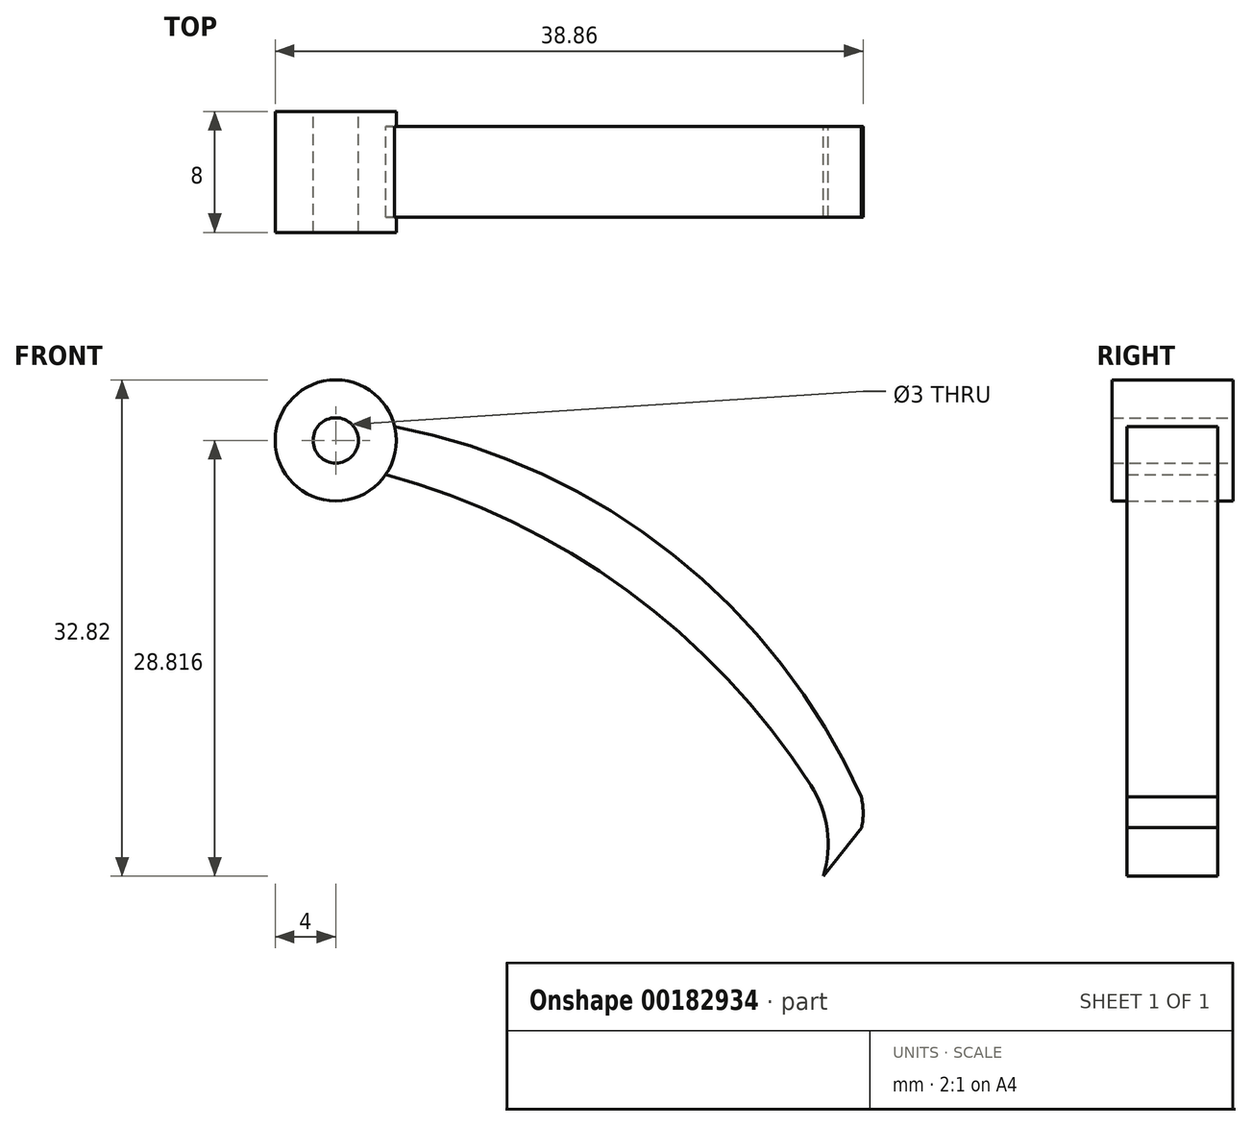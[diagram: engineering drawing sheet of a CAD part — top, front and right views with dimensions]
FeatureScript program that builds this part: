
annotation { "Feature Type Name" : "Feature", "Feature Type Description" : "" }
export const myFeature = defineFeature(function(context is Context, id is Id, definition is map)
    precondition{}
    {
        {
            var Q0;
            Q0=qCreatedBy(makeId("Front.planeOp"),FACE);
            var sketch = newSketch(context, id + "F0", { "sketchPlane" : qUnion([Q0])});
            skPoint(sketch, "E0.center", {"position": v(-0.03, 0) * mm});
            skLineSegment(sketch, "E1", {"start": v(0, 0) * mm, "end": v(-0.03, 0) * mm});
            skLineSegment(sketch, "E2", {"start": v(-0.03, 0) * mm, "end": v(0, 0.04) * mm});
            skArc(sketch, "E3", {"start": v(31.4, 46.86) * mm, "mid": v(19.25, 59.73) * mm, "end": v(3.3, 67.38) * mm});
            skPoint(sketch, "E3.startSnap0", {"position": v(33.76, 42.76) * mm});
            skLineSegment(sketch, "E4", {"start": v(32.2, 40.8) * mm, "end": v(32.2, 40.82) * mm});
            skLineSegment(sketch, "E5.trimOffspring", {"start": v(32.2, 40.8) * mm, "end": v(34.76, 44.04) * mm});
            skPoint(sketch, "E6.orphan", {"position": v(33.76, 42.78) * mm});
            skArc(sketch, "E7", {"start": v(32.2, 40.8) * mm, "mid": v(32.49, 43.92) * mm, "end": v(31.4, 46.86) * mm});
            skArc(sketch, "E8", {"start": v(34.76, 44.04) * mm, "mid": v(34.86, 45.06) * mm, "end": v(34.73, 46.08) * mm});
            skArc(sketch, "E9.trimOffspring", {"start": v(34.73, 46.08) * mm, "mid": v(22.3, 62.1) * mm, "end": v(3.9, 70.57) * mm});
            skCircle(sketch, "E10", {"center": v(0, 69.65) * mm, "radius": 4 * mm});
            skCircle(sketch, "E11", {"center": v(0, 69.65) * mm, "radius": 1.5 * mm});
            skSolve(sketch);
        }
        {
            var Q0;
            {var subQ2=sQuery(id+"F0.wireOp",EDGE,"E3");Q0=makeQuery(id+"F0.imprint","IMPRINT",FACE,{"disambiguationData":[TD([[makeQuery(id+"F0.imprint","IMPRINT",EDGE,{"derivedFrom":subQ2}),-1.0]])]});}
            extrude(context, id + "F1", {"entities" : qUnion([Q0]), "endBound" : BoundingType.SYMMETRIC, "depth" : 6 * mm});
        }
        {
            var Q0;
            Q0=makeQuery(id+"F0.imprint","IMPRINT",FACE,{"disambiguationData":[TD([[makeQuery(id+"F0.imprint","IMPRINT",EDGE,{"derivedFrom":sQuery(id+"F0.wireOp",EDGE,"E11")}),-1.0]])]});
            extrude(context, id + "F2", {"entities" : qUnion([Q0]), "operationType" : NewBodyOperationType.ADD, "endBound" : BoundingType.SYMMETRIC, "depth" : 8 * mm});
        }
    });
